# Revit family: 797060001_Valvula De Bola Manija Mariposa
name_source: partatom
category: Pipe Accessories
units: mm (PartAtom-declared; Revit-internal decimal feet)

## family parameters
Always vertical = Yes
Cut with Voids When Loaded = No
OmniClass Number = 23.27.31.15
OmniClass Title = Ball Valves
Part Type = Valve - Breaks Into
Round Connector Dimension = Use Diameter
Shared = No
Work Plane-Based = No

## types (1)
- 797060001 (1/2")
    A = 51.5 mm  [stored 0.168963 ft]
    C1 = 10 mm  [stored 0.0328084 ft]
    C2 = 10.5 mm  [stored 0.0344488 ft]
    Creado por = BIMBAU
    Default Elevation = 0 mm  [stored 0 ft]
    Description = Para trabajo pesado, presión de trabajo manométrica máxima: 435 PSI
    Diametro nominal = 12.7 mm  [stored 0.0416667 ft]
    F1 = 12.7 mm  [stored 0.0416667 ft]
    F2 = 12.7 mm  [stored 0.0416667 ft]
    Fecha de creación = 12/03/2021
    G = 4 mm  [stored 0.0131234 ft]
    H = 38 mm
    H Nut = 10.5 mm  [stored 0.0344488 ft]
    IR-Nut = 5.5 mm  [stored 0.0180446 ft]
    L = 55 mm
    Manufacturer = Grival
    Material = Corona_Bronce
    Material 2 = Corona_Bronce Rojo
    Max Pressure = 40.0 bar
    Min Pressure = 25.0 bar
    Model = Valvula de control
    OR-Nut = 12.5 mm  [stored 0.0410105 ft]
    Outside Radius = 12.5 mm  [stored 0.0410105 ft]
    Presión de servicio = Presión de trabajo manométrica máxima del agua 3000 kPa
(345 psi) Presión mínima recomendada 138 kPa (20 psi).
    Referencia = 797060001
    Temperatura de uso = De 4° C A 16° C (40° F y 61° F).
    Vida útil = 5.000 ciclos a 138 kPa

note: [stored X ft] marks values corroborated as IEEE doubles in the binary element streams (Revit-internal decimal feet)

## geometry (parser evidence)
native form markers: Sweep x8
no freeform markers — native parametric forms only
